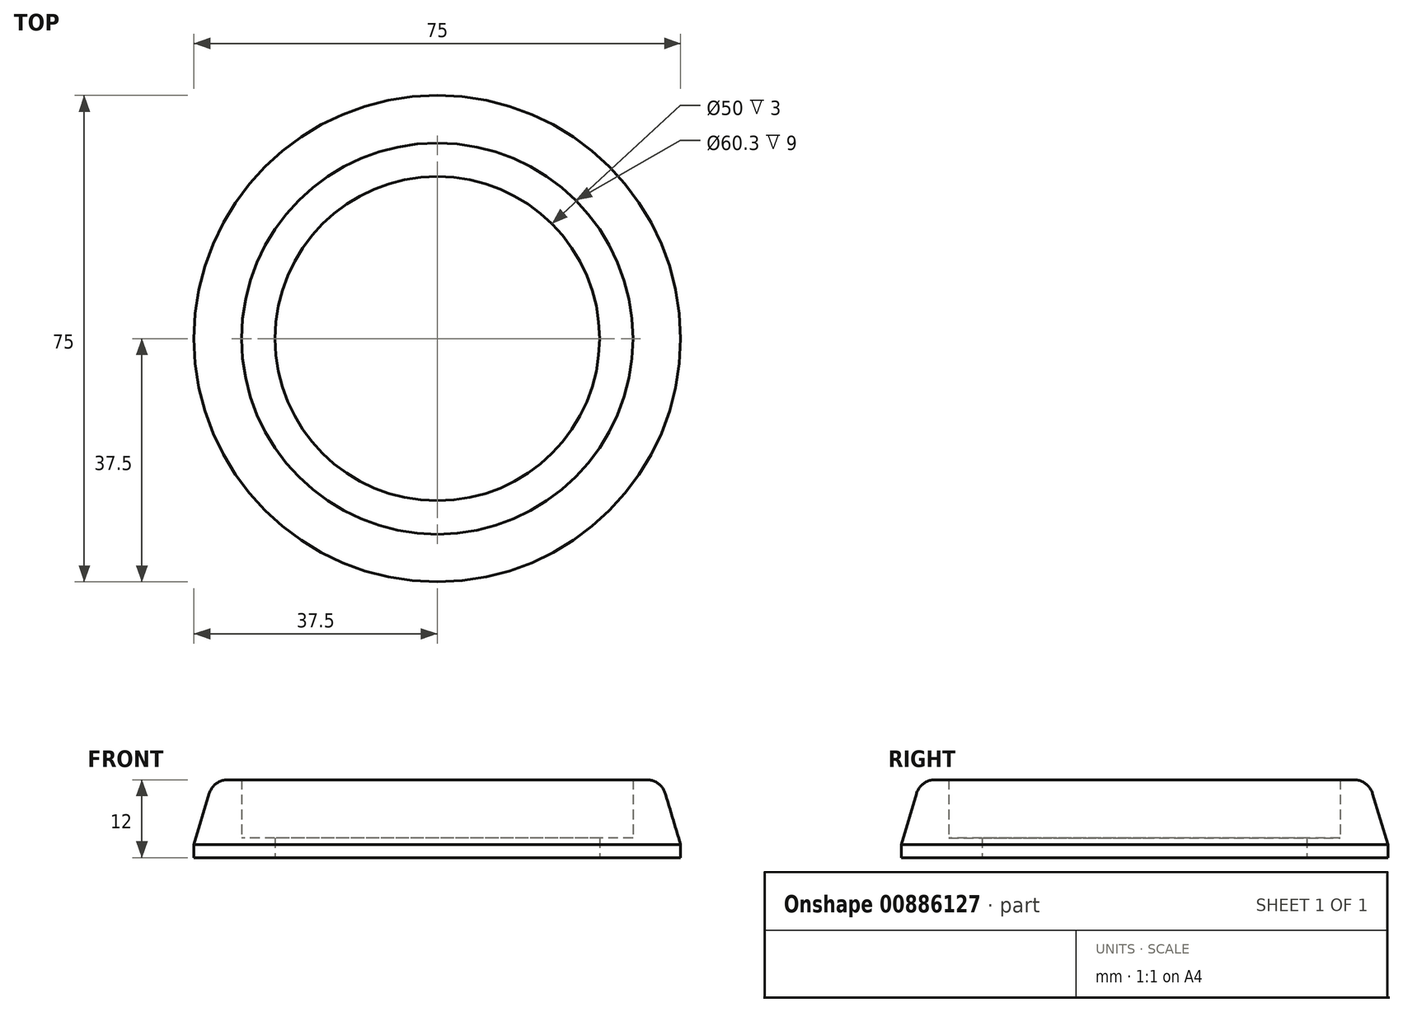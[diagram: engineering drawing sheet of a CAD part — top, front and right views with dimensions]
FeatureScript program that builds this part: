
annotation { "Feature Type Name" : "Feature", "Feature Type Description" : "" }
export const myFeature = defineFeature(function(context is Context, id is Id, definition is map)
    precondition{}
    {
        {
            var Q0;
            Q0=qCreatedBy(makeId("Top.planeOp"),FACE);
            var sketch = newSketch(context, id + "F0", { "sketchPlane" : qUnion([Q0])});
            skCircle(sketch, "E0", {"center": v(0, 0) * mm, "radius": 30.15 * mm});
            skCircle(sketch, "E1", {"center": v(0, 0) * mm, "radius": 37.5 * mm});
            skCircle(sketch, "E2", {"center": v(0, 0) * mm, "radius": 25 * mm});
            skSolve(sketch);
        }
        {
            var Q0;
            Q0=makeQuery(id+"F0.imprint","IMPRINT",FACE,{"disambiguationData":[TD([[makeQuery(id+"F0.imprint","IMPRINT",EDGE,{"derivedFrom":sQuery(id+"F0.wireOp",EDGE,"E0")}),-1.0]])]});
            var Q1;
            Q1=makeQuery(id+"F0.imprint","IMPRINT",FACE,{"disambiguationData":[TD([[makeQuery(id+"F0.imprint","IMPRINT",EDGE,{"derivedFrom":sQuery(id+"F0.wireOp",EDGE,"E0")}),1.0]])]});
            var Q2;
            Q2=sQuery(id+"F0.wireOp",EDGE,"E1");
            extrude(context, id + "F1", {"entities" : qUnion([Q0, Q1]), "surfaceEntities" : qUnion([Q2]), "depth" : 3 * mm, "offsetDistance" : 25 * mm});
        }
        {
            var Q0;
            Q0=makeQuery(id+"F0.imprint","IMPRINT",FACE,{"disambiguationData":[TD([[makeQuery(id+"F0.imprint","IMPRINT",EDGE,{"derivedFrom":sQuery(id+"F0.wireOp",EDGE,"E0")}),-1.0]])]});
            extrude(context, id + "F2", {"entities" : qUnion([Q0]), "operationType" : NewBodyOperationType.ADD, "depth" : 12 * mm, "offsetDistance" : 25 * mm});
        }
        {
            var Q0;
            Q0=makeQuery(id+"F2.opExtrude","CAP_EDGE",EDGE,{"disambiguationData":[OSD([sQuery(id+"F0.wireOp",EDGE,"E1")])],"isStart":false});
            chamfer(context, id + "F3", {"entities" : qUnion([Q0]), "chamferType" : ChamferType.TWO_OFFSETS, "width1" : 3 * mm, "oppositeDirection" : false, "width2" : 10 * mm, "tangentPropagation" : true});
        }
        {
            var Q0;
            {var subQ0=sQuery(id+"F0.wireOp",EDGE,"E1");Q0=makeQuery(id+"F3.opChamfer","BLEND_EDGE",EDGE,{"blendedFrom":[makeQuery(id+"F2.opExtrude","CAP_EDGE",EDGE,{"disambiguationData":[OSD([subQ0])],"isStart":false}),makeQuery(id+"F2.opExtrude","CAP_FACE",FACE,{"disambiguationData":[OSD([sQuery(id+"F0.wireOp",EDGE,"E0"),subQ0])],"isStart":false})],"blendedInto":[makeQuery(id+"F2.opExtrude","CAP_FACE",FACE,{"disambiguationData":[OSD([sQuery(id+"F0.wireOp",EDGE,"E0"),subQ0])],"isStart":false})]});}
            fillet(context, id + "F4", {"entities" : qUnion([Q0]), "radius" : 3 * mm, "tangentPropagation" : true, "allowEdgeOverflow" : false});
        }
    });
